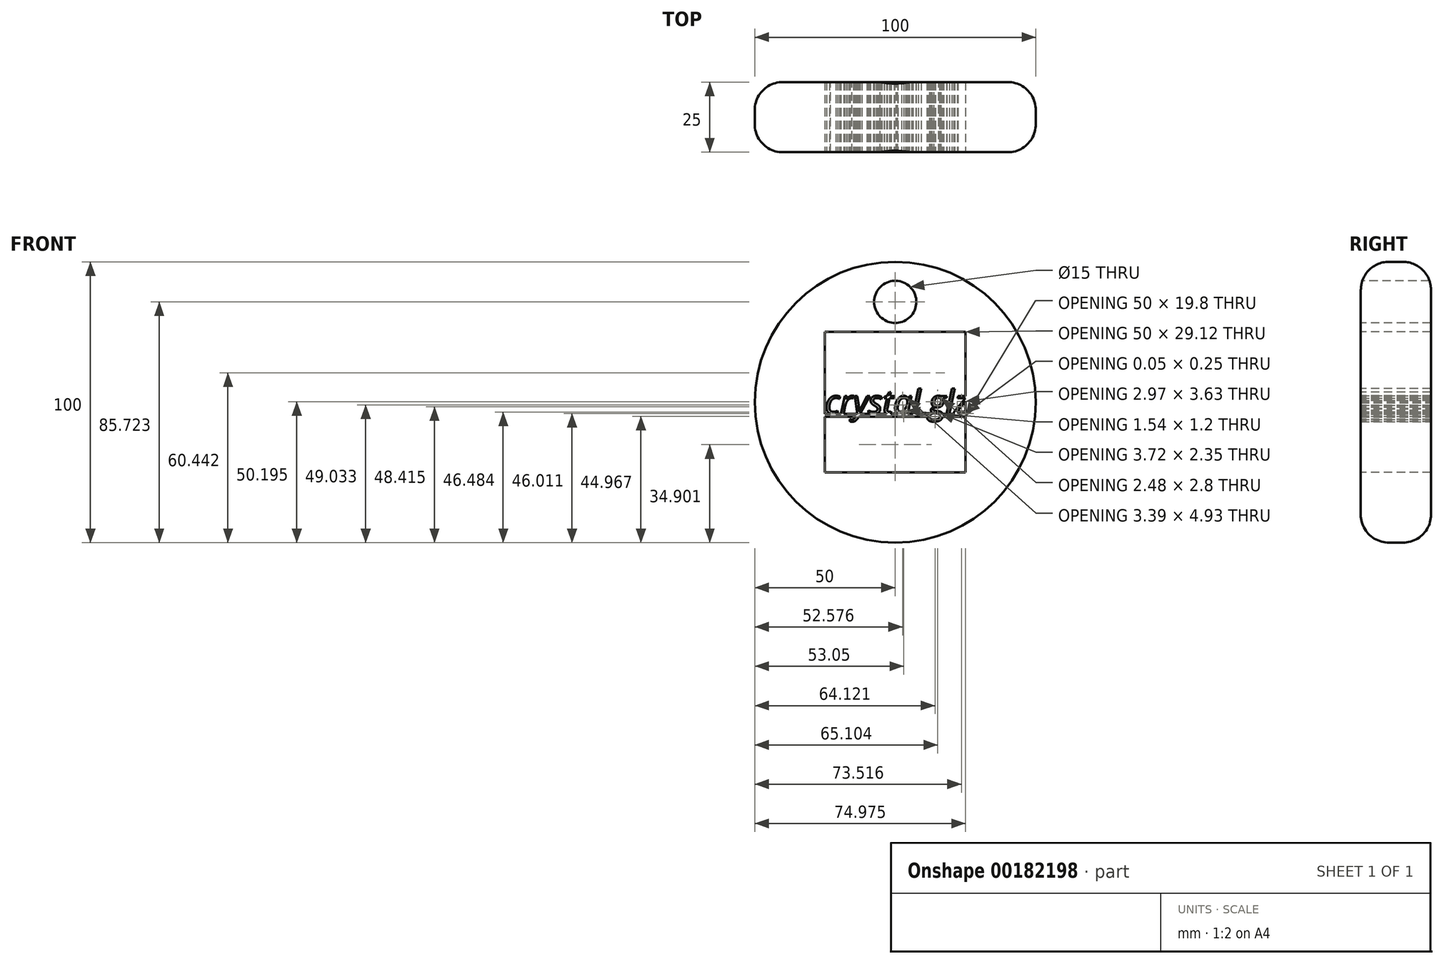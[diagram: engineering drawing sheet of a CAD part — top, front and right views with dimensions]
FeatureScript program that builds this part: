
annotation { "Feature Type Name" : "Feature", "Feature Type Description" : "" }
export const myFeature = defineFeature(function(context is Context, id is Id, definition is map)
    precondition{}
    {
        {
            var Q0;
            Q0=qCreatedBy(makeId("Front.planeOp"),FACE);
            var sketch = newSketch(context, id + "F0", { "sketchPlane" : qUnion([Q0])});
            skCircle(sketch, "E0", {"center": v(0, 0) * mm, "radius": 50 * mm});
            skSolve(sketch);
        }
        {
            var Q0;
            Q0 = qSketchRegion(id + "F0", true);
            extrude(context, id + "F1", {"entities" : qUnion([Q0]), "depth" : 25 * mm});
        }
        {
            var Q0;
            Q0=makeQuery(id+"F1.opExtrude","CAP_FACE",FACE,{"disambiguationData":[OSD([sQuery(id+"F0.wireOp",EDGE,"E0")])],"isStart":false});
            var sketch = newSketch(context, id + "F2", { "sketchPlane" : qUnion([Q0])});
            skLineSegment(sketch, "E1.bottom", {"start": v(25, 25) * mm, "end": v(-25, 25) * mm});
            skLineSegment(sketch, "E1.top", {"start": v(25, -25) * mm, "end": v(-25, -25) * mm});
            skLineSegment(sketch, "E1.left", {"start": v(25, 25) * mm, "end": v(25, -25) * mm});
            skLineSegment(sketch, "E1.right", {"start": v(-25, 25) * mm, "end": v(-25, -25) * mm});
            skPoint(sketch, "E1.middle", {"position": v(0, 0) * mm});
            skSolve(sketch);
        }
        {
            var Q0;
            Q0 = qSketchRegion(id + "F2", true);
            extrude(context, id + "F3", {"entities" : qUnion([Q0]), "operationType" : NewBodyOperationType.REMOVE, "oppositeDirection" : true, "depth" : 25 * mm});
        }
        {
            var Q0;
            Q0=makeQuery(id+"F1.opExtrude","CAP_FACE",FACE,{"disambiguationData":[OSD([sQuery(id+"F0.wireOp",EDGE,"E0")])],"isStart":false});
            var sketch = newSketch(context, id + "F4", { "sketchPlane" : qUnion([Q0])});
            skText(sketch, "E2", { "text": "crystal glz\n\n\n", "fontName": "OpenSans-Italic.ttf"});
            skLineSegment(sketch, "E3.bottom", {"start": v(-25, -4.12) * mm, "end": v(25, -4.12) * mm});
            skLineSegment(sketch, "E3.top", {"start": v(-25, -5.2) * mm, "end": v(25, -5.2) * mm});
            skLineSegment(sketch, "E3.left", {"start": v(-25, -4.12) * mm, "end": v(-25, -5.2) * mm});
            skLineSegment(sketch, "E3.right", {"start": v(25, -4.12) * mm, "end": v(25, -5.2) * mm});
            const initialGuessF4  = {"E2": [-0.025, -0.00412, 1, 0, 0.0085]};
            skSetInitialGuess(sketch, initialGuessF4);
            skSolve(sketch);
        }
        {
            var Q0;
            Q0 = qSketchRegion(id + "F4", true);
            extrude(context, id + "F5", {"entities" : qUnion([Q0]), "operationType" : NewBodyOperationType.ADD, "oppositeDirection" : true, "depth" : 25 * mm});
        }
        {
            var Q0;
            Q0=makeQuery(id+"F1.opExtrude","CAP_EDGE",EDGE,{"disambiguationData":[OSD([sQuery(id+"F0.wireOp",EDGE,"E0")])],"isStart":true});
            var Q1;
            Q1=makeQuery(id+"F1.opExtrude","CAP_EDGE",EDGE,{"disambiguationData":[OSD([sQuery(id+"F0.wireOp",EDGE,"E0")])],"isStart":false});
            fillet(context, id + "F6", {"entities" : qUnion([Q0, Q1]), "radius" : 10 * mm, "tangentPropagation" : true, "allowEdgeOverflow" : false});
        }
        {
            var Q0;
            Q0=makeQuery(id+"F5.boolean.opBoolean","MERGE",FACE,{"derivedFrom":[makeQuery(id+"F1.opExtrude","CAP_FACE",FACE,{"disambiguationData":[OSD([sQuery(id+"F0.wireOp",EDGE,"E0")])],"isStart":false}),makeQuery(id+"F5.opExtrude","CAP_FACE",FACE,{"disambiguationData":[OSD([sQuery(id+"F4.wireOp",EDGE,"E2.sketch_text.stroke-0"),sQuery(id+"F4.wireOp",EDGE,"E2.sketch_text.stroke-1"),sQuery(id+"F4.wireOp",EDGE,"E2.sketch_text.stroke-2"),sQuery(id+"F4.wireOp",EDGE,"E2.sketch_text.stroke-3"),sQuery(id+"F4.wireOp",EDGE,"E2.sketch_text.stroke-4"),sQuery(id+"F4.wireOp",EDGE,"E2.sketch_text.stroke-5"),sQuery(id+"F4.wireOp",EDGE,"E2.sketch_text.stroke-6"),sQuery(id+"F4.wireOp",EDGE,"E2.sketch_text.stroke-7"),sQuery(id+"F4.wireOp",EDGE,"E2.sketch_text.stroke-8"),sQuery(id+"F4.wireOp",EDGE,"E2.sketch_text.stroke-9"),sQuery(id+"F4.wireOp",EDGE,"E2.sketch_text.stroke-10"),sQuery(id+"F4.wireOp",EDGE,"E2.sketch_text.stroke-11"),sQuery(id+"F4.wireOp",EDGE,"E2.sketch_text.stroke-12"),sQuery(id+"F4.wireOp",EDGE,"E2.sketch_text.stroke-13"),sQuery(id+"F4.wireOp",EDGE,"E2.sketch_text.stroke-14"),sQuery(id+"F4.wireOp",EDGE,"E2.sketch_text.stroke-15"),sQuery(id+"F4.wireOp",EDGE,"E2.sketch_text.stroke-16"),sQuery(id+"F4.wireOp",EDGE,"E2.sketch_text.stroke-17"),sQuery(id+"F4.wireOp",EDGE,"E2.sketch_text.stroke-18"),sQuery(id+"F4.wireOp",EDGE,"E2.sketch_text.stroke-19"),sQuery(id+"F4.wireOp",EDGE,"E2.sketch_text.stroke-20"),sQuery(id+"F4.wireOp",EDGE,"E2.sketch_text.stroke-21"),sQuery(id+"F4.wireOp",EDGE,"E2.sketch_text.stroke-22"),sQuery(id+"F4.wireOp",EDGE,"E2.sketch_text.stroke-23"),sQuery(id+"F4.wireOp",EDGE,"E2.sketch_text.stroke-25"),sQuery(id+"F4.wireOp",EDGE,"E2.sketch_text.stroke-26"),sQuery(id+"F4.wireOp",EDGE,"E2.sketch_text.stroke-27"),sQuery(id+"F4.wireOp",EDGE,"E2.sketch_text.stroke-28"),sQuery(id+"F4.wireOp",EDGE,"E2.sketch_text.stroke-29"),sQuery(id+"F4.wireOp",EDGE,"E2.sketch_text.stroke-30"),sQuery(id+"F4.wireOp",EDGE,"E2.sketch_text.stroke-31"),sQuery(id+"F4.wireOp",EDGE,"E2.sketch_text.stroke-32"),sQuery(id+"F4.wireOp",EDGE,"E2.sketch_text.stroke-33"),sQuery(id+"F4.wireOp",EDGE,"E2.sketch_text.stroke-34"),sQuery(id+"F4.wireOp",EDGE,"E2.sketch_text.stroke-35"),sQuery(id+"F4.wireOp",EDGE,"E2.sketch_text.stroke-36"),sQuery(id+"F4.wireOp",EDGE,"E2.sketch_text.stroke-37"),sQuery(id+"F4.wireOp",EDGE,"E2.sketch_text.stroke-38"),sQuery(id+"F4.wireOp",EDGE,"E2.sketch_text.stroke-39"),sQuery(id+"F4.wireOp",EDGE,"E2.sketch_text.stroke-40"),sQuery(id+"F4.wireOp",EDGE,"E2.sketch_text.stroke-41"),sQuery(id+"F4.wireOp",EDGE,"E2.sketch_text.stroke-42"),sQuery(id+"F4.wireOp",EDGE,"E2.sketch_text.stroke-43"),sQuery(id+"F4.wireOp",EDGE,"E2.sketch_text.stroke-44"),sQuery(id+"F4.wireOp",EDGE,"E2.sketch_text.stroke-45"),sQuery(id+"F4.wireOp",EDGE,"E2.sketch_text.stroke-46"),sQuery(id+"F4.wireOp",EDGE,"E2.sketch_text.stroke-47"),sQuery(id+"F4.wireOp",EDGE,"E2.sketch_text.stroke-48"),sQuery(id+"F4.wireOp",EDGE,"E2.sketch_text.stroke-50"),sQuery(id+"F4.wireOp",EDGE,"E2.sketch_text.stroke-51"),sQuery(id+"F4.wireOp",EDGE,"E2.sketch_text.stroke-52"),sQuery(id+"F4.wireOp",EDGE,"E2.sketch_text.stroke-53"),sQuery(id+"F4.wireOp",EDGE,"E2.sketch_text.stroke-54"),sQuery(id+"F4.wireOp",EDGE,"E2.sketch_text.stroke-55"),sQuery(id+"F4.wireOp",EDGE,"E2.sketch_text.stroke-56"),sQuery(id+"F4.wireOp",EDGE,"E2.sketch_text.stroke-57"),sQuery(id+"F4.wireOp",EDGE,"E2.sketch_text.stroke-58"),sQuery(id+"F4.wireOp",EDGE,"E2.sketch_text.stroke-59"),sQuery(id+"F4.wireOp",EDGE,"E2.sketch_text.stroke-60"),sQuery(id+"F4.wireOp",EDGE,"E2.sketch_text.stroke-61"),sQuery(id+"F4.wireOp",EDGE,"E2.sketch_text.stroke-62"),sQuery(id+"F4.wireOp",EDGE,"E2.sketch_text.stroke-63"),sQuery(id+"F4.wireOp",EDGE,"E2.sketch_text.stroke-64"),sQuery(id+"F4.wireOp",EDGE,"E2.sketch_text.stroke-65"),sQuery(id+"F4.wireOp",EDGE,"E2.sketch_text.stroke-66"),sQuery(id+"F4.wireOp",EDGE,"E2.sketch_text.stroke-67"),sQuery(id+"F4.wireOp",EDGE,"E2.sketch_text.stroke-68"),sQuery(id+"F4.wireOp",EDGE,"E2.sketch_text.stroke-69"),sQuery(id+"F4.wireOp",EDGE,"E2.sketch_text.stroke-70"),sQuery(id+"F4.wireOp",EDGE,"E2.sketch_text.stroke-71"),sQuery(id+"F4.wireOp",EDGE,"E2.sketch_text.stroke-72"),sQuery(id+"F4.wireOp",EDGE,"E2.sketch_text.stroke-73"),sQuery(id+"F4.wireOp",EDGE,"E2.sketch_text.stroke-74"),sQuery(id+"F4.wireOp",EDGE,"E2.sketch_text.stroke-75"),sQuery(id+"F4.wireOp",EDGE,"E2.sketch_text.stroke-76"),sQuery(id+"F4.wireOp",EDGE,"E2.sketch_text.stroke-77"),sQuery(id+"F4.wireOp",EDGE,"E2.sketch_text.stroke-78"),sQuery(id+"F4.wireOp",EDGE,"E2.sketch_text.stroke-80"),sQuery(id+"F4.wireOp",EDGE,"E2.sketch_text.stroke-81"),sQuery(id+"F4.wireOp",EDGE,"E2.sketch_text.stroke-82"),sQuery(id+"F4.wireOp",EDGE,"E2.sketch_text.stroke-83"),sQuery(id+"F4.wireOp",EDGE,"E2.sketch_text.stroke-84"),sQuery(id+"F4.wireOp",EDGE,"E2.sketch_text.stroke-85"),sQuery(id+"F4.wireOp",EDGE,"E2.sketch_text.stroke-86"),sQuery(id+"F4.wireOp",EDGE,"E2.sketch_text.stroke-87"),sQuery(id+"F4.wireOp",EDGE,"E2.sketch_text.stroke-88"),sQuery(id+"F4.wireOp",EDGE,"E2.sketch_text.stroke-89"),sQuery(id+"F4.wireOp",EDGE,"E2.sketch_text.stroke-90"),sQuery(id+"F4.wireOp",EDGE,"E2.sketch_text.stroke-91"),sQuery(id+"F4.wireOp",EDGE,"E2.sketch_text.stroke-92"),sQuery(id+"F4.wireOp",EDGE,"E2.sketch_text.stroke-93"),sQuery(id+"F4.wireOp",EDGE,"E2.sketch_text.stroke-94"),sQuery(id+"F4.wireOp",EDGE,"E2.sketch_text.stroke-95"),sQuery(id+"F4.wireOp",EDGE,"E2.sketch_text.stroke-96"),sQuery(id+"F4.wireOp",EDGE,"E2.sketch_text.stroke-97"),sQuery(id+"F4.wireOp",EDGE,"E2.sketch_text.stroke-98"),sQuery(id+"F4.wireOp",EDGE,"E2.sketch_text.stroke-99"),sQuery(id+"F4.wireOp",EDGE,"E2.sketch_text.stroke-100"),sQuery(id+"F4.wireOp",EDGE,"E2.sketch_text.stroke-101"),sQuery(id+"F4.wireOp",EDGE,"E2.sketch_text.stroke-102"),sQuery(id+"F4.wireOp",EDGE,"E2.sketch_text.stroke-104"),sQuery(id+"F4.wireOp",EDGE,"E2.sketch_text.stroke-105"),sQuery(id+"F4.wireOp",EDGE,"E2.sketch_text.stroke-106"),sQuery(id+"F4.wireOp",EDGE,"E2.sketch_text.stroke-107"),sQuery(id+"F4.wireOp",EDGE,"E2.sketch_text.stroke-108"),sQuery(id+"F4.wireOp",EDGE,"E2.sketch_text.stroke-109"),sQuery(id+"F4.wireOp",EDGE,"E2.sketch_text.stroke-110"),sQuery(id+"F4.wireOp",EDGE,"E2.sketch_text.stroke-111"),sQuery(id+"F4.wireOp",EDGE,"E2.sketch_text.stroke-112"),sQuery(id+"F4.wireOp",EDGE,"E2.sketch_text.stroke-113"),sQuery(id+"F4.wireOp",EDGE,"E2.sketch_text.stroke-114"),sQuery(id+"F4.wireOp",EDGE,"E2.sketch_text.stroke-115"),sQuery(id+"F4.wireOp",EDGE,"E2.sketch_text.stroke-116"),sQuery(id+"F4.wireOp",EDGE,"E2.sketch_text.stroke-117"),sQuery(id+"F4.wireOp",EDGE,"E2.sketch_text.stroke-118"),sQuery(id+"F4.wireOp",EDGE,"E2.sketch_text.stroke-119"),sQuery(id+"F4.wireOp",EDGE,"E2.sketch_text.stroke-120"),sQuery(id+"F4.wireOp",EDGE,"E2.sketch_text.stroke-121"),sQuery(id+"F4.wireOp",EDGE,"E2.sketch_text.stroke-123"),sQuery(id+"F4.wireOp",EDGE,"E2.sketch_text.stroke-124"),sQuery(id+"F4.wireOp",EDGE,"E2.sketch_text.stroke-125"),sQuery(id+"F4.wireOp",EDGE,"E2.sketch_text.stroke-126"),sQuery(id+"F4.wireOp",EDGE,"E2.sketch_text.stroke-127"),sQuery(id+"F4.wireOp",EDGE,"E2.sketch_text.stroke-128"),sQuery(id+"F4.wireOp",EDGE,"E2.sketch_text.stroke-129"),sQuery(id+"F4.wireOp",EDGE,"E2.sketch_text.stroke-130"),sQuery(id+"F4.wireOp",EDGE,"E2.sketch_text.stroke-131"),sQuery(id+"F4.wireOp",EDGE,"E2.sketch_text.stroke-132"),sQuery(id+"F4.wireOp",EDGE,"E2.sketch_text.stroke-133"),sQuery(id+"F4.wireOp",EDGE,"E2.sketch_text.stroke-134"),sQuery(id+"F4.wireOp",EDGE,"E2.sketch_text.stroke-135"),sQuery(id+"F4.wireOp",EDGE,"E2.sketch_text.stroke-136"),sQuery(id+"F4.wireOp",EDGE,"E2.sketch_text.stroke-137"),sQuery(id+"F4.wireOp",EDGE,"E2.sketch_text.stroke-138"),sQuery(id+"F4.wireOp",EDGE,"E2.sketch_text.stroke-139"),sQuery(id+"F4.wireOp",EDGE,"E2.sketch_text.stroke-140"),sQuery(id+"F4.wireOp",EDGE,"E2.sketch_text.stroke-141"),sQuery(id+"F4.wireOp",EDGE,"E2.sketch_text.stroke-142"),sQuery(id+"F4.wireOp",EDGE,"E2.sketch_text.stroke-143"),sQuery(id+"F4.wireOp",EDGE,"E2.sketch_text.stroke-144"),sQuery(id+"F4.wireOp",EDGE,"E2.sketch_text.stroke-145"),sQuery(id+"F4.wireOp",EDGE,"E2.sketch_text.stroke-146"),sQuery(id+"F4.wireOp",EDGE,"E2.sketch_text.stroke-147"),sQuery(id+"F4.wireOp",EDGE,"E2.sketch_text.stroke-148"),sQuery(id+"F4.wireOp",EDGE,"E2.sketch_text.stroke-149"),sQuery(id+"F4.wireOp",EDGE,"E2.sketch_text.stroke-150"),sQuery(id+"F4.wireOp",EDGE,"E2.sketch_text.stroke-151"),sQuery(id+"F4.wireOp",EDGE,"E2.sketch_text.stroke-152"),sQuery(id+"F4.wireOp",EDGE,"E2.sketch_text.stroke-153"),sQuery(id+"F4.wireOp",EDGE,"E2.sketch_text.stroke-154"),sQuery(id+"F4.wireOp",EDGE,"E2.sketch_text.stroke-155"),sQuery(id+"F4.wireOp",EDGE,"E2.sketch_text.stroke-156"),sQuery(id+"F4.wireOp",EDGE,"E2.sketch_text.stroke-157"),sQuery(id+"F4.wireOp",EDGE,"E2.sketch_text.stroke-158"),sQuery(id+"F4.wireOp",EDGE,"E2.sketch_text.stroke-159"),sQuery(id+"F4.wireOp",EDGE,"E2.sketch_text.stroke-160"),sQuery(id+"F4.wireOp",EDGE,"E2.sketch_text.stroke-161"),sQuery(id+"F4.wireOp",EDGE,"E2.sketch_text.stroke-162"),sQuery(id+"F4.wireOp",EDGE,"E2.sketch_text.stroke-163"),sQuery(id+"F4.wireOp",EDGE,"E2.sketch_text.stroke-164"),sQuery(id+"F4.wireOp",EDGE,"E2.sketch_text.stroke-165"),sQuery(id+"F4.wireOp",EDGE,"E2.sketch_text.stroke-166"),sQuery(id+"F4.wireOp",EDGE,"E2.sketch_text.stroke-167"),sQuery(id+"F4.wireOp",EDGE,"E2.sketch_text.stroke-168"),sQuery(id+"F4.wireOp",EDGE,"E2.sketch_text.stroke-169"),sQuery(id+"F4.wireOp",EDGE,"E2.sketch_text.stroke-170"),sQuery(id+"F4.wireOp",EDGE,"E2.sketch_text.stroke-171"),sQuery(id+"F4.wireOp",EDGE,"E2.sketch_text.stroke-173"),sQuery(id+"F4.wireOp",EDGE,"E2.sketch_text.stroke-174"),sQuery(id+"F4.wireOp",EDGE,"E2.sketch_text.stroke-175"),sQuery(id+"F4.wireOp",EDGE,"E2.sketch_text.stroke-177"),sQuery(id+"F4.wireOp",EDGE,"E2.sketch_text.stroke-178"),sQuery(id+"F4.wireOp",EDGE,"E2.sketch_text.stroke-179"),sQuery(id+"F4.wireOp",EDGE,"E2.sketch_text.stroke-180"),sQuery(id+"F4.wireOp",EDGE,"E2.sketch_text.stroke-181"),sQuery(id+"F4.wireOp",EDGE,"E2.sketch_text.stroke-182"),sQuery(id+"F4.wireOp",EDGE,"E2.sketch_text.stroke-183"),sQuery(id+"F4.wireOp",EDGE,"E2.sketch_text.stroke-184"),sQuery(id+"F4.wireOp",EDGE,"E2.sketch_text.stroke-185"),sQuery(id+"F4.wireOp",EDGE,"E3.bottom"),sQuery(id+"F4.wireOp",EDGE,"E3.top"),sQuery(id+"F4.wireOp",EDGE,"E3.left"),sQuery(id+"F4.wireOp",EDGE,"E3.right")])],"isStart":true})]});
            var sketch = newSketch(context, id + "F7", { "sketchPlane" : qUnion([Q0])});
            skCircle(sketch, "E4", {"center": v(0, 35.72) * mm, "radius": 7.5 * mm});
            skPoint(sketch, "E5", {"position": v(0, 25) * mm});
            skSolve(sketch);
        }
        {
            var Q0;
            Q0 = qSketchRegion(id + "F7", true);
            extrude(context, id + "F8", {"entities" : qUnion([Q0]), "operationType" : NewBodyOperationType.REMOVE, "oppositeDirection" : true, "depth" : 26 * mm});
        }
    });
